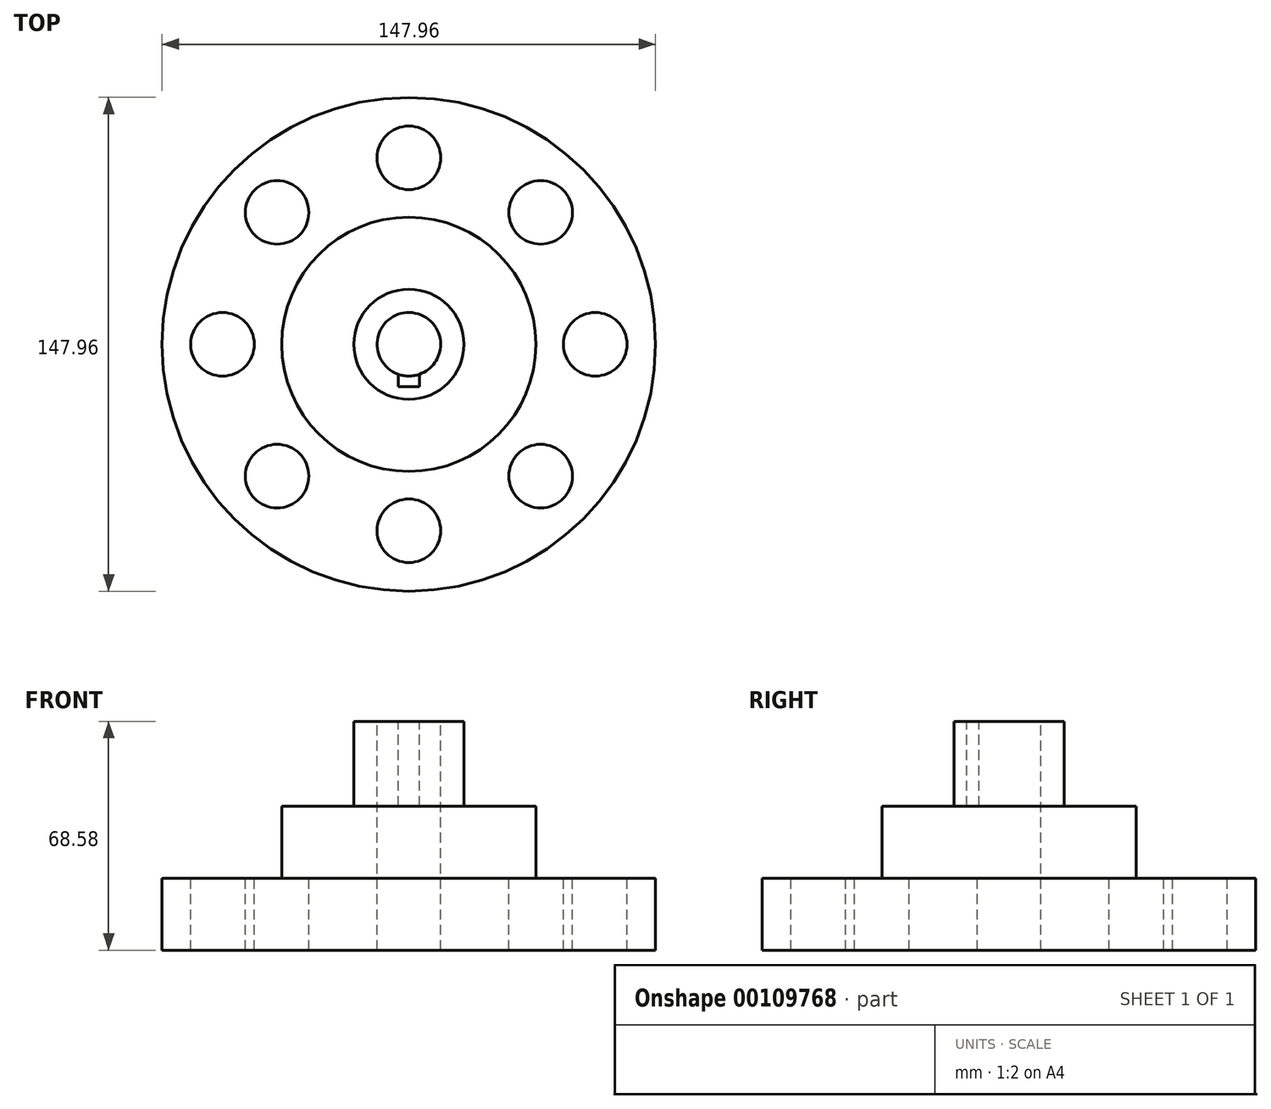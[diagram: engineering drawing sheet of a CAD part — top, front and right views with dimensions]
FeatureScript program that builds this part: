
annotation { "Feature Type Name" : "Feature", "Feature Type Description" : "" }
export const myFeature = defineFeature(function(context is Context, id is Id, definition is map)
    precondition{}
    {
        {
            var Q0;
            Q0=qCreatedBy(makeId("Top.planeOp"),FACE);
            var sketch = newSketch(context, id + "F0", { "sketchPlane" : qUnion([Q0])});
            skCircle(sketch, "E0", {"center": v(0, 0) * mm, "radius": 73.98 * mm});
            skSolve(sketch);
        }
        {
            var Q0;
            Q0=makeQuery(id+"F0.imprint","IMPRINT",FACE,{"disambiguationData":[TD([[makeQuery(id+"F0.imprint","IMPRINT",EDGE,{"derivedFrom":sQuery(id+"F0.wireOp",EDGE,"E0")}),1.0]])]});
            extrude(context, id + "F1", {"entities" : qUnion([Q0]), "depth" : 21.59 * mm});
        }
        {
            var Q0;
            Q0=makeQuery(id+"F1.opExtrude","CAP_FACE",FACE,{"disambiguationData":[OSD([sQuery(id+"F0.wireOp",EDGE,"E0")])],"isStart":false});
            var sketch = newSketch(context, id + "F2", { "sketchPlane" : qUnion([Q0])});
            skCircle(sketch, "E1", {"center": v(0, 0) * mm, "radius": 55.88 * mm});
            skLineSegment(sketch, "E2", {"start": v(0, 0) * mm, "end": v(0, 55.88) * mm});
            skCircle(sketch, "E3", {"center": v(0, 55.88) * mm, "radius": 9.53 * mm});
            skLineSegment(sketch, "E4", {"start": v(0, 0) * mm, "end": v(55.88, 0) * mm});
            skCircle(sketch, "E5", {"center": v(55.88, 0) * mm, "radius": 9.53 * mm});
            skLineSegment(sketch, "E6", {"start": v(0, 0) * mm, "end": v(0, -55.88) * mm});
            skCircle(sketch, "E7", {"center": v(0, -55.88) * mm, "radius": 9.53 * mm});
            skLineSegment(sketch, "E8", {"start": v(0, 0) * mm, "end": v(-55.88, 0) * mm});
            skCircle(sketch, "E9", {"center": v(-55.88, 0) * mm, "radius": 9.53 * mm});
            skLineSegment(sketch, "E10", {"start": v(0, 0) * mm, "end": v(39.51, 39.51) * mm});
            skCircle(sketch, "E11", {"center": v(39.51, 39.51) * mm, "radius": 9.53 * mm});
            skLineSegment(sketch, "E12", {"start": v(0, 0) * mm, "end": v(39.51, -39.51) * mm});
            skLineSegment(sketch, "E13", {"start": v(0, 0) * mm, "end": v(-39.51, -39.51) * mm});
            skLineSegment(sketch, "E14", {"start": v(0, 0) * mm, "end": v(-39.51, 39.51) * mm});
            skCircle(sketch, "E15", {"center": v(39.51, -39.51) * mm, "radius": 9.53 * mm});
            skCircle(sketch, "E16", {"center": v(-39.51, -39.51) * mm, "radius": 9.53 * mm});
            skCircle(sketch, "E17", {"center": v(-39.51, 39.51) * mm, "radius": 9.53 * mm});
            skSolve(sketch);
        }
        {
            var Q0;
            {var subQ0=sQuery(id+"F2.wireOp",EDGE,"E1");var subQ1=makeQuery(id+"F2.imprint","INTERSECT",VERTEX,{"derivedFrom":[subQ0,sQuery(id+"F2.wireOp",EDGE,"E14")]});Q0=makeQuery(id+"F2.imprint","IMPRINT",FACE,{"disambiguationData":[TD([[makeQuery(id+"F2.imprint","IMPRINT",EDGE,{"disambiguationData":[TD([[subQ1,1.0]])],"derivedFrom":subQ0}),-1.0]])]});}
            var Q1;
            {var subQ0=sQuery(id+"F2.wireOp",EDGE,"E14");var subQ1=sQuery(id+"F2.wireOp",EDGE,"E1");var subQ2=makeQuery(id+"F2.imprint","INTERSECT",VERTEX,{"derivedFrom":[subQ1,subQ0]});Q1=makeQuery(id+"F2.imprint","IMPRINT",FACE,{"disambiguationData":[TD([[makeQuery(id+"F2.imprint","IMPRINT",EDGE,{"disambiguationData":[TD([[subQ2,-1.0]])],"derivedFrom":subQ1}),1.0]])]});}
            var Q2;
            {var subQ0=sQuery(id+"F2.wireOp",EDGE,"E14");var subQ1=sQuery(id+"F2.wireOp",EDGE,"E1");var subQ2=makeQuery(id+"F2.imprint","INTERSECT",VERTEX,{"derivedFrom":[subQ1,subQ0]});Q2=makeQuery(id+"F2.imprint","IMPRINT",FACE,{"disambiguationData":[TD([[makeQuery(id+"F2.imprint","IMPRINT",EDGE,{"disambiguationData":[TD([[subQ2,1.0]])],"derivedFrom":subQ1}),1.0]])]});}
            var Q3;
            {var subQ0=sQuery(id+"F2.wireOp",EDGE,"E1");var subQ1=makeQuery(id+"F2.imprint","INTERSECT",VERTEX,{"derivedFrom":[subQ0,sQuery(id+"F2.wireOp",EDGE,"E2")]});Q3=makeQuery(id+"F2.imprint","IMPRINT",FACE,{"disambiguationData":[TD([[makeQuery(id+"F2.imprint","IMPRINT",EDGE,{"disambiguationData":[TD([[subQ1,1.0]])],"derivedFrom":subQ0}),-1.0]])]});}
            var Q4;
            {var subQ0=sQuery(id+"F2.wireOp",EDGE,"E2");var subQ1=sQuery(id+"F2.wireOp",EDGE,"E1");var subQ2=makeQuery(id+"F2.imprint","INTERSECT",VERTEX,{"derivedFrom":[subQ1,subQ0]});Q4=makeQuery(id+"F2.imprint","IMPRINT",FACE,{"disambiguationData":[TD([[makeQuery(id+"F2.imprint","IMPRINT",EDGE,{"disambiguationData":[TD([[subQ2,-1.0]])],"derivedFrom":subQ1}),1.0]])]});}
            var Q5;
            {var subQ0=sQuery(id+"F2.wireOp",EDGE,"E2");var subQ1=sQuery(id+"F2.wireOp",EDGE,"E1");var subQ2=makeQuery(id+"F2.imprint","INTERSECT",VERTEX,{"derivedFrom":[subQ1,subQ0]});Q5=makeQuery(id+"F2.imprint","IMPRINT",FACE,{"disambiguationData":[TD([[makeQuery(id+"F2.imprint","IMPRINT",EDGE,{"disambiguationData":[TD([[subQ2,1.0]])],"derivedFrom":subQ1}),1.0]])]});}
            var Q6;
            {var subQ0=sQuery(id+"F2.wireOp",EDGE,"E10");var subQ1=sQuery(id+"F2.wireOp",EDGE,"E1");var subQ2=makeQuery(id+"F2.imprint","INTERSECT",VERTEX,{"derivedFrom":[subQ1,subQ0]});Q6=makeQuery(id+"F2.imprint","IMPRINT",FACE,{"disambiguationData":[TD([[makeQuery(id+"F2.imprint","IMPRINT",EDGE,{"disambiguationData":[TD([[subQ2,-1.0]])],"derivedFrom":subQ1}),1.0]])]});}
            var Q7;
            {var subQ0=sQuery(id+"F2.wireOp",EDGE,"E10");var subQ1=sQuery(id+"F2.wireOp",EDGE,"E1");var subQ2=makeQuery(id+"F2.imprint","INTERSECT",VERTEX,{"derivedFrom":[subQ1,subQ0]});Q7=makeQuery(id+"F2.imprint","IMPRINT",FACE,{"disambiguationData":[TD([[makeQuery(id+"F2.imprint","IMPRINT",EDGE,{"disambiguationData":[TD([[subQ2,1.0]])],"derivedFrom":subQ1}),1.0]])]});}
            var Q8;
            {var subQ0=sQuery(id+"F2.wireOp",EDGE,"E1");var subQ1=makeQuery(id+"F2.imprint","INTERSECT",VERTEX,{"derivedFrom":[subQ0,sQuery(id+"F2.wireOp",EDGE,"E10")]});Q8=makeQuery(id+"F2.imprint","IMPRINT",FACE,{"disambiguationData":[TD([[makeQuery(id+"F2.imprint","IMPRINT",EDGE,{"disambiguationData":[TD([[subQ1,1.0]])],"derivedFrom":subQ0}),-1.0]])]});}
            var Q9;
            {var subQ0=sQuery(id+"F2.wireOp",EDGE,"E4");var subQ1=sQuery(id+"F2.wireOp",EDGE,"E1");var subQ2=makeQuery(id+"F2.imprint","INTERSECT",VERTEX,{"derivedFrom":[subQ1,subQ0]});Q9=makeQuery(id+"F2.imprint","IMPRINT",FACE,{"disambiguationData":[TD([[makeQuery(id+"F2.imprint","IMPRINT",EDGE,{"disambiguationData":[TD([[subQ2,-1.0]])],"derivedFrom":subQ1}),1.0]])]});}
            var Q10;
            {var subQ0=sQuery(id+"F2.wireOp",EDGE,"E1");var subQ1=makeQuery(id+"F2.imprint","INTERSECT",VERTEX,{"derivedFrom":[subQ0,sQuery(id+"F2.wireOp",EDGE,"E4")]});Q10=makeQuery(id+"F2.imprint","IMPRINT",FACE,{"disambiguationData":[TD([[makeQuery(id+"F2.imprint","IMPRINT",EDGE,{"disambiguationData":[TD([[subQ1,-1.0]])],"derivedFrom":subQ0}),-1.0]])]});}
            var Q11;
            {var subQ0=sQuery(id+"F2.wireOp",EDGE,"E4");var subQ1=sQuery(id+"F2.wireOp",EDGE,"E1");var subQ2=makeQuery(id+"F2.imprint","INTERSECT",VERTEX,{"derivedFrom":[subQ1,subQ0]});Q11=makeQuery(id+"F2.imprint","IMPRINT",FACE,{"disambiguationData":[TD([[makeQuery(id+"F2.imprint","IMPRINT",EDGE,{"disambiguationData":[TD([[subQ2,1.0]])],"derivedFrom":subQ1}),1.0]])]});}
            var Q12;
            {var subQ0=sQuery(id+"F2.wireOp",EDGE,"E12");var subQ1=sQuery(id+"F2.wireOp",EDGE,"E1");var subQ2=makeQuery(id+"F2.imprint","INTERSECT",VERTEX,{"derivedFrom":[subQ1,subQ0]});Q12=makeQuery(id+"F2.imprint","IMPRINT",FACE,{"disambiguationData":[TD([[makeQuery(id+"F2.imprint","IMPRINT",EDGE,{"disambiguationData":[TD([[subQ2,-1.0]])],"derivedFrom":subQ1}),1.0]])]});}
            var Q13;
            {var subQ0=sQuery(id+"F2.wireOp",EDGE,"E12");var subQ1=sQuery(id+"F2.wireOp",EDGE,"E1");var subQ2=makeQuery(id+"F2.imprint","INTERSECT",VERTEX,{"derivedFrom":[subQ1,subQ0]});Q13=makeQuery(id+"F2.imprint","IMPRINT",FACE,{"disambiguationData":[TD([[makeQuery(id+"F2.imprint","IMPRINT",EDGE,{"disambiguationData":[TD([[subQ2,1.0]])],"derivedFrom":subQ1}),1.0]])]});}
            var Q14;
            {var subQ0=sQuery(id+"F2.wireOp",EDGE,"E1");var subQ1=makeQuery(id+"F2.imprint","INTERSECT",VERTEX,{"derivedFrom":[subQ0,sQuery(id+"F2.wireOp",EDGE,"E12")]});Q14=makeQuery(id+"F2.imprint","IMPRINT",FACE,{"disambiguationData":[TD([[makeQuery(id+"F2.imprint","IMPRINT",EDGE,{"disambiguationData":[TD([[subQ1,1.0]])],"derivedFrom":subQ0}),-1.0]])]});}
            var Q15;
            {var subQ0=sQuery(id+"F2.wireOp",EDGE,"E6");var subQ1=sQuery(id+"F2.wireOp",EDGE,"E1");var subQ2=makeQuery(id+"F2.imprint","INTERSECT",VERTEX,{"derivedFrom":[subQ1,subQ0]});Q15=makeQuery(id+"F2.imprint","IMPRINT",FACE,{"disambiguationData":[TD([[makeQuery(id+"F2.imprint","IMPRINT",EDGE,{"disambiguationData":[TD([[subQ2,1.0]])],"derivedFrom":subQ1}),1.0]])]});}
            var Q16;
            {var subQ0=sQuery(id+"F2.wireOp",EDGE,"E6");var subQ1=sQuery(id+"F2.wireOp",EDGE,"E1");var subQ2=makeQuery(id+"F2.imprint","INTERSECT",VERTEX,{"derivedFrom":[subQ1,subQ0]});Q16=makeQuery(id+"F2.imprint","IMPRINT",FACE,{"disambiguationData":[TD([[makeQuery(id+"F2.imprint","IMPRINT",EDGE,{"disambiguationData":[TD([[subQ2,-1.0]])],"derivedFrom":subQ1}),1.0]])]});}
            var Q17;
            {var subQ0=sQuery(id+"F2.wireOp",EDGE,"E1");var subQ1=makeQuery(id+"F2.imprint","INTERSECT",VERTEX,{"derivedFrom":[subQ0,sQuery(id+"F2.wireOp",EDGE,"E6")]});Q17=makeQuery(id+"F2.imprint","IMPRINT",FACE,{"disambiguationData":[TD([[makeQuery(id+"F2.imprint","IMPRINT",EDGE,{"disambiguationData":[TD([[subQ1,1.0]])],"derivedFrom":subQ0}),-1.0]])]});}
            var Q18;
            {var subQ0=sQuery(id+"F2.wireOp",EDGE,"E1");var subQ1=makeQuery(id+"F2.imprint","INTERSECT",VERTEX,{"derivedFrom":[subQ0,sQuery(id+"F2.wireOp",EDGE,"E13")]});Q18=makeQuery(id+"F2.imprint","IMPRINT",FACE,{"disambiguationData":[TD([[makeQuery(id+"F2.imprint","IMPRINT",EDGE,{"disambiguationData":[TD([[subQ1,1.0]])],"derivedFrom":subQ0}),-1.0]])]});}
            var Q19;
            {var subQ0=sQuery(id+"F2.wireOp",EDGE,"E13");var subQ1=sQuery(id+"F2.wireOp",EDGE,"E1");var subQ2=makeQuery(id+"F2.imprint","INTERSECT",VERTEX,{"derivedFrom":[subQ1,subQ0]});Q19=makeQuery(id+"F2.imprint","IMPRINT",FACE,{"disambiguationData":[TD([[makeQuery(id+"F2.imprint","IMPRINT",EDGE,{"disambiguationData":[TD([[subQ2,1.0]])],"derivedFrom":subQ1}),1.0]])]});}
            var Q20;
            {var subQ0=sQuery(id+"F2.wireOp",EDGE,"E13");var subQ1=sQuery(id+"F2.wireOp",EDGE,"E1");var subQ2=makeQuery(id+"F2.imprint","INTERSECT",VERTEX,{"derivedFrom":[subQ1,subQ0]});Q20=makeQuery(id+"F2.imprint","IMPRINT",FACE,{"disambiguationData":[TD([[makeQuery(id+"F2.imprint","IMPRINT",EDGE,{"disambiguationData":[TD([[subQ2,-1.0]])],"derivedFrom":subQ1}),1.0]])]});}
            var Q21;
            {var subQ0=sQuery(id+"F2.wireOp",EDGE,"E1");var subQ1=makeQuery(id+"F2.imprint","INTERSECT",VERTEX,{"derivedFrom":[subQ0,sQuery(id+"F2.wireOp",EDGE,"E8")]});Q21=makeQuery(id+"F2.imprint","IMPRINT",FACE,{"disambiguationData":[TD([[makeQuery(id+"F2.imprint","IMPRINT",EDGE,{"disambiguationData":[TD([[subQ1,1.0]])],"derivedFrom":subQ0}),-1.0]])]});}
            var Q22;
            {var subQ0=sQuery(id+"F2.wireOp",EDGE,"E8");var subQ1=sQuery(id+"F2.wireOp",EDGE,"E1");var subQ2=makeQuery(id+"F2.imprint","INTERSECT",VERTEX,{"derivedFrom":[subQ1,subQ0]});Q22=makeQuery(id+"F2.imprint","IMPRINT",FACE,{"disambiguationData":[TD([[makeQuery(id+"F2.imprint","IMPRINT",EDGE,{"disambiguationData":[TD([[subQ2,-1.0]])],"derivedFrom":subQ1}),1.0]])]});}
            var Q23;
            {var subQ0=sQuery(id+"F2.wireOp",EDGE,"E8");var subQ1=sQuery(id+"F2.wireOp",EDGE,"E1");var subQ2=makeQuery(id+"F2.imprint","INTERSECT",VERTEX,{"derivedFrom":[subQ1,subQ0]});Q23=makeQuery(id+"F2.imprint","IMPRINT",FACE,{"disambiguationData":[TD([[makeQuery(id+"F2.imprint","IMPRINT",EDGE,{"disambiguationData":[TD([[subQ2,1.0]])],"derivedFrom":subQ1}),1.0]])]});}
            extrude(context, id + "F3", {"entities" : qUnion([Q0, Q1, Q2, Q3, Q4, Q5, Q6, Q7, Q8, Q9, Q10, Q11, Q12, Q13, Q14, Q15, Q16, Q17, Q18, Q19, Q20, Q21, Q22, Q23]), "operationType" : NewBodyOperationType.REMOVE, "endBound" : BoundingType.THROUGH_ALL, "oppositeDirection" : true, "depth" : 25.4 * mm});
        }
        {
            var Q0;
            Q0=makeQuery(id+"F1.opExtrude","CAP_FACE",FACE,{"disambiguationData":[OSD([sQuery(id+"F0.wireOp",EDGE,"E0")])],"isStart":false});
            var sketch = newSketch(context, id + "F4", { "sketchPlane" : qUnion([Q0])});
            skCircle(sketch, "E18", {"center": v(0, 0) * mm, "radius": 38.1 * mm});
            skSolve(sketch);
        }
        {
            var Q0;
            Q0=makeQuery(id+"F4.imprint","IMPRINT",FACE,{"disambiguationData":[TD([[makeQuery(id+"F4.imprint","IMPRINT",EDGE,{"derivedFrom":sQuery(id+"F4.wireOp",EDGE,"E18")}),1.0]])]});
            extrude(context, id + "F5", {"entities" : qUnion([Q0]), "operationType" : NewBodyOperationType.ADD, "depth" : 21.59 * mm});
        }
        {
            var Q0;
            Q0=makeQuery(id+"F5.opExtrude","CAP_FACE",FACE,{"disambiguationData":[OSD([sQuery(id+"F4.wireOp",EDGE,"E18")])],"isStart":false});
            var sketch = newSketch(context, id + "F6", { "sketchPlane" : qUnion([Q0])});
            skCircle(sketch, "E19", {"center": v(0, 0) * mm, "radius": 16.51 * mm});
            skSolve(sketch);
        }
        {
            var Q0;
            Q0=makeQuery(id+"F6.imprint","IMPRINT",FACE,{"disambiguationData":[TD([[makeQuery(id+"F6.imprint","IMPRINT",EDGE,{"derivedFrom":sQuery(id+"F6.wireOp",EDGE,"E19")}),1.0]])]});
            extrude(context, id + "F7", {"entities" : qUnion([Q0]), "operationType" : NewBodyOperationType.ADD, "depth" : 25.4 * mm});
        }
        {
            var Q0;
            Q0=makeQuery(id+"F7.opExtrude","CAP_FACE",FACE,{"disambiguationData":[OSD([sQuery(id+"F6.wireOp",EDGE,"E19")])],"isStart":false});
            var sketch = newSketch(context, id + "F8", { "sketchPlane" : qUnion([Q0])});
            skCircle(sketch, "E20", {"center": v(0, 0) * mm, "radius": 12.7 * mm});
            skSolve(sketch);
        }
        {
            var Q0;
            Q0=sQuery(id+"F8.wireOp",VERTEX,"E20.center");
            var Q1;
            Q1=makeQuery(id+"F1.opExtrude","SWEPT_BODY",BODY,{"disambiguationData":[OSD([sQuery(id+"F0.wireOp",EDGE,"E0")])]});
            hole(context, id + "F9", {"style" : HoleStyle.SIMPLE, "endStyle" : HoleEndStyle.THROUGH, "holeDiameter" : 19.05 * mm, "locations" : qUnion([Q0]), "scope" : qUnion([Q1]), "isTappedThrough" : true});
        }
        {
            var Q0;
            Q0=makeQuery(id+"F7.opExtrude","CAP_FACE",FACE,{"disambiguationData":[OSD([sQuery(id+"F6.wireOp",EDGE,"E19")])],"isStart":false});
            var sketch = newSketch(context, id + "F10", { "sketchPlane" : qUnion([Q0])});
            skLineSegment(sketch, "E21.bottom", {"start": v(3.17, -12.7) * mm, "end": v(-3.18, -12.7) * mm});
            skLineSegment(sketch, "E21.top", {"start": v(3.18, -6.35) * mm, "end": v(-3.18, -6.35) * mm});
            skLineSegment(sketch, "E21.left", {"start": v(3.17, -12.7) * mm, "end": v(3.18, -6.35) * mm});
            skLineSegment(sketch, "E21.right", {"start": v(-3.18, -12.7) * mm, "end": v(-3.18, -6.35) * mm});
            skPoint(sketch, "E21.middle", {"position": v(0, -9.53) * mm});
            skSolve(sketch);
        }
        {
            var Q0;
            {var subQ0=sQuery(id+"F10.wireOp",EDGE,"E21.bottom");Q0=makeQuery(id+"F10.imprint","IMPRINT",FACE,{"disambiguationData":[TD([[makeQuery(id+"F10.imprint","IMPRINT",EDGE,{"derivedFrom":subQ0}),-1.0]])]});}
            extrude(context, id + "F11", {"entities" : qUnion([Q0]), "operationType" : NewBodyOperationType.REMOVE, "oppositeDirection" : true, "depth" : 25.4 * mm});
        }
    });
